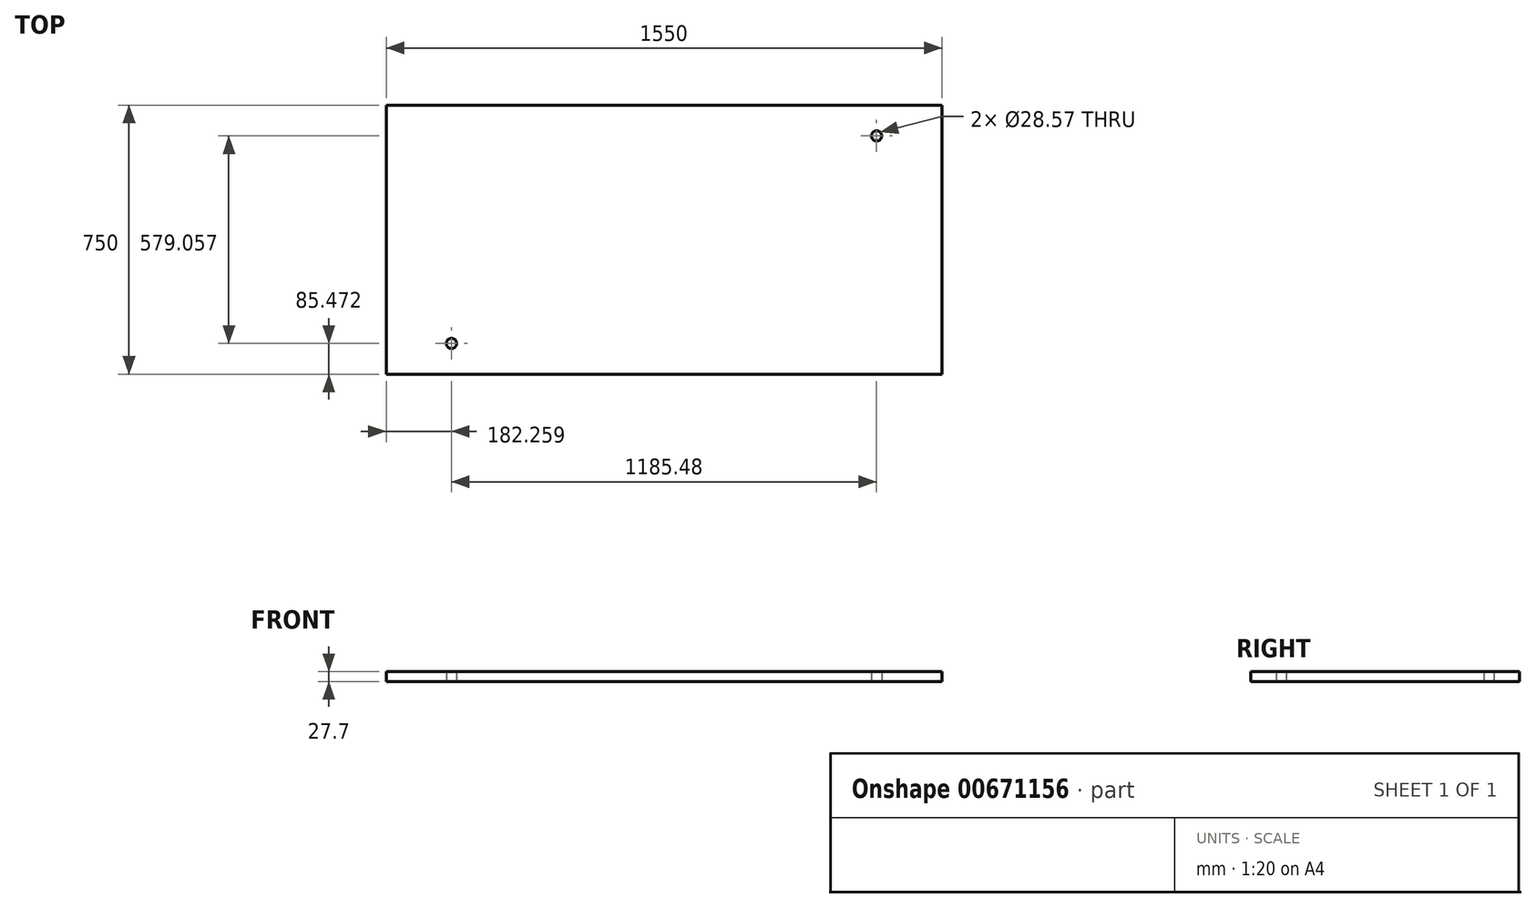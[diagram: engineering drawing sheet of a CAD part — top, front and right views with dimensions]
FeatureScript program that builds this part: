
annotation { "Feature Type Name" : "Feature", "Feature Type Description" : "" }
export const myFeature = defineFeature(function(context is Context, id is Id, definition is map)
    precondition{}
    {
        {
            assignVariable(context, id + "F0", {"name" : "tableThickness", "anyValue" : 28.2});
        }
        {
            var Q0;
            Q0=qCreatedBy(makeId("Top.planeOp"),FACE);
            var sketch = newSketch(context, id + "F1", { "sketchPlane" : qUnion([Q0])});
            skLineSegment(sketch, "E0.bottom", {"start": v(775, -375) * mm, "end": v(-775, -375) * mm});
            skLineSegment(sketch, "E0.top", {"start": v(775, 375) * mm, "end": v(-775, 375) * mm});
            skLineSegment(sketch, "E0.left", {"start": v(775, -375) * mm, "end": v(775, 375) * mm});
            skLineSegment(sketch, "E0.right", {"start": v(-775, -375) * mm, "end": v(-775, 375) * mm});
            skPoint(sketch, "E0.middle", {"position": v(0, 0) * mm});
            skLineSegment(sketch, "E1", {"start": v(0, 375) * mm, "end": v(0, -375) * mm, "construction": true});
            skLineSegment(sketch, "E2", {"start": v(775, 0) * mm, "end": v(-775, 0) * mm, "construction": true});
            skCircle(sketch, "E3", {"center": v(-592.74, 289.53) * mm, "radius": 12.5 * mm, "construction": true});
            skCircle(sketch, "E4.MirrorC", {"center": v(-592.74, -289.53) * mm, "radius": 12.5 * mm, "construction": true});
            skCircle(sketch, "E5.MirrorC", {"center": v(592.74, -289.53) * mm, "radius": 12.5 * mm, "construction": true});
            skCircle(sketch, "E6.MirrorC", {"center": v(592.74, 289.53) * mm, "radius": 12.5 * mm, "construction": true});
            skCircle(sketch, "E7", {"center": v(-592.74, 289.53) * mm, "radius": 14.29 * mm});
            skCircle(sketch, "E8.MirrorC", {"center": v(-592.74, -289.53) * mm, "radius": 14.29 * mm});
            skCircle(sketch, "E9.MirrorC", {"center": v(592.74, -289.53) * mm, "radius": 14.29 * mm});
            skCircle(sketch, "E10.MirrorC", {"center": v(592.74, 289.53) * mm, "radius": 14.29 * mm});
            skLineSegment(sketch, "E11", {"start": v(-592.74, -289.53) * mm, "end": v(-592.74, -277.02) * mm, "construction": true});
            skLineSegment(sketch, "E12", {"start": v(-592.74, 289.53) * mm, "end": v(-592.74, 277.02) * mm, "construction": true});
            skLineSegment(sketch, "E13", {"start": v(-592.74, 289.53) * mm, "end": v(-580.23, 289.53) * mm, "construction": true});
            skLineSegment(sketch, "E14", {"start": v(580.23, 289.53) * mm, "end": v(592.74, 289.53) * mm, "construction": true});
            skSolve(sketch);
        }
        {
            var Q0;
            Q0=makeQuery(id+"F1.imprint","IMPRINT",FACE,{"disambiguationData":[TD([[makeQuery(id+"F1.imprint","IMPRINT",EDGE,{"derivedFrom":sQuery(id+"F1.wireOp",EDGE,"E0.bottom")}),-1.0]])]});
            var Q1;
            Q1=makeQuery(id+"F1.imprint","IMPRINT",FACE,{"disambiguationData":[TD([[makeQuery(id+"F1.imprint","IMPRINT",EDGE,{"derivedFrom":sQuery(id+"F1.wireOp",EDGE,"E9.MirrorC")}),1.0]])]});
            var Q2;
            Q2=makeQuery(id+"F1.imprint","IMPRINT",FACE,{"disambiguationData":[TD([[makeQuery(id+"F1.imprint","IMPRINT",EDGE,{"derivedFrom":sQuery(id+"F1.wireOp",EDGE,"E10.MirrorC")}),-1.0]])]});
            var Q3;
            Q3=makeQuery(id+"F1.imprint","IMPRINT",FACE,{"disambiguationData":[TD([[makeQuery(id+"F1.imprint","IMPRINT",EDGE,{"derivedFrom":sQuery(id+"F1.wireOp",EDGE,"E7")}),1.0]])]});
            var Q4;
            Q4=makeQuery(id+"F1.imprint","IMPRINT",FACE,{"disambiguationData":[TD([[makeQuery(id+"F1.imprint","IMPRINT",EDGE,{"derivedFrom":sQuery(id+"F1.wireOp",EDGE,"E8.MirrorC")}),-1.0]])]});
            extrude(context, id + "F2", {"entities" : qUnion([Q0, Q1, Q2, Q3, Q4]), "depth" : getVariable(context, 'tableThickness') * mm, "offsetDistance" : 25.4 * mm});
        }
        {
            assignVariable(context, id + "F3", {"name" : "holeDepth", "anyValue" : 1 / 2});
        }
        {
            var Q0;
            Q0=makeQuery(id+"F1.imprint","IMPRINT",FACE,{"disambiguationData":[TD([[makeQuery(id+"F1.imprint","IMPRINT",EDGE,{"derivedFrom":sQuery(id+"F1.wireOp",EDGE,"E10.MirrorC")}),-1.0]])]});
            var Q1;
            Q1=makeQuery(id+"F1.imprint","IMPRINT",FACE,{"disambiguationData":[TD([[makeQuery(id+"F1.imprint","IMPRINT",EDGE,{"derivedFrom":sQuery(id+"F1.wireOp",EDGE,"E9.MirrorC")}),1.0]])]});
            var Q2;
            Q2=makeQuery(id+"F1.imprint","IMPRINT",FACE,{"disambiguationData":[TD([[makeQuery(id+"F1.imprint","IMPRINT",EDGE,{"derivedFrom":sQuery(id+"F1.wireOp",EDGE,"E8.MirrorC")}),-1.0]])]});
            var Q3;
            Q3=makeQuery(id+"F1.imprint","IMPRINT",FACE,{"disambiguationData":[TD([[makeQuery(id+"F1.imprint","IMPRINT",EDGE,{"derivedFrom":sQuery(id+"F1.wireOp",EDGE,"E7")}),1.0]])]});
            extrude(context, id + "F4", {"entities" : qUnion([Q0, Q1, Q2, Q3]), "operationType" : NewBodyOperationType.REMOVE, "depth" : (getVariable(context, 'holeDepth')) * mm, "offsetDistance" : 25.4 * mm});
        }
    });
